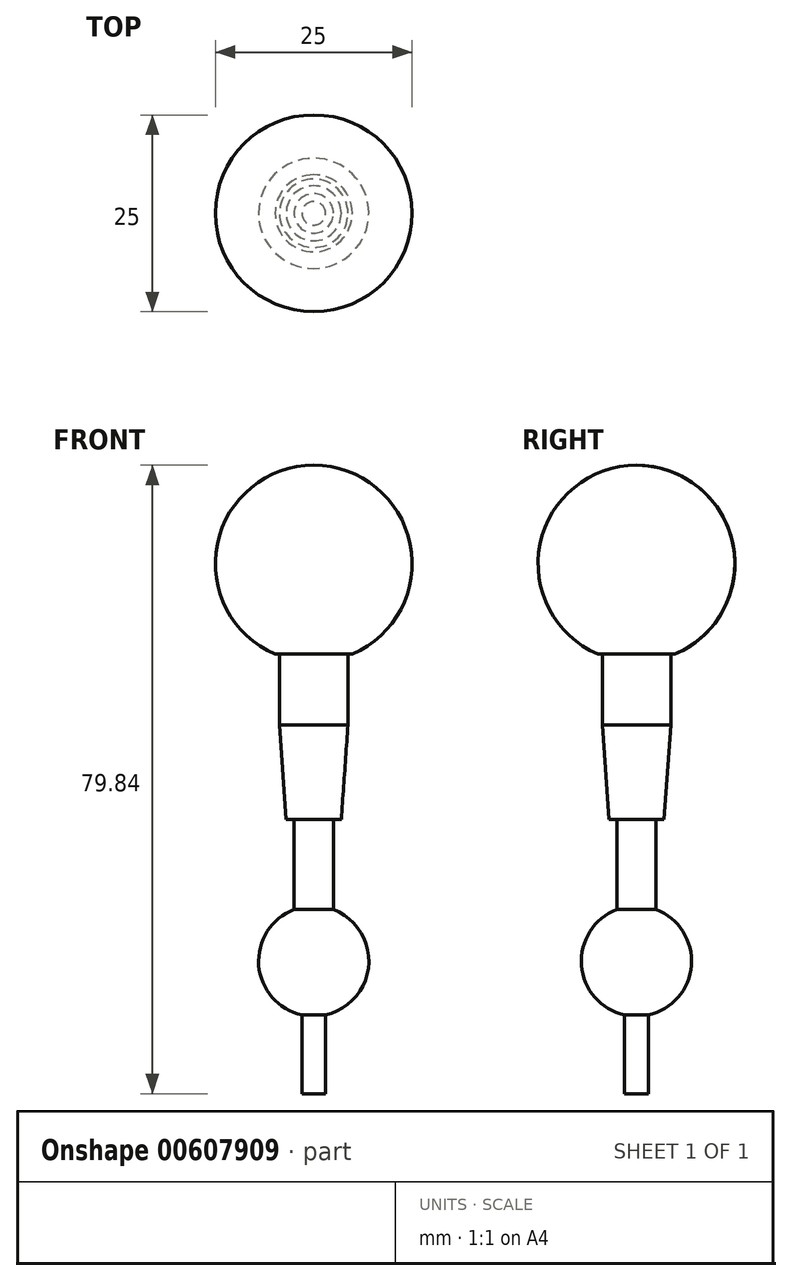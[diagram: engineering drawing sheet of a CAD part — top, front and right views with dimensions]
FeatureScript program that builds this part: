
annotation { "Feature Type Name" : "Feature", "Feature Type Description" : "" }
export const myFeature = defineFeature(function(context is Context, id is Id, definition is map)
    precondition{}
    {
        {
            var Q0;
            Q0=qCreatedBy(makeId("Right.planeOp"),FACE);
            var sketch = newSketch(context, id + "F0", { "sketchPlane" : qUnion([Q0])});
            skLineSegment(sketch, "E0", {"start": v(0, 70) * mm, "end": v(0, 0) * mm});
            skArc(sketch, "E1", {"start": v(0, 70) * mm, "mid": v(12.5, 57.5) * mm, "end": v(0, 45) * mm});
            skLineSegment(sketch, "E2", {"start": v(0, 46) * mm, "end": v(4.9, 46) * mm});
            skLineSegment(sketch, "E3", {"start": v(4.35, 46) * mm, "end": v(4.35, 37) * mm});
            skLineSegment(sketch, "E4", {"start": v(4.35, 37) * mm, "end": v(3.5, 25) * mm});
            skLineSegment(sketch, "E5", {"start": v(3.5, 25) * mm, "end": v(0, 25) * mm});
            skLineSegment(sketch, "E6", {"start": v(2.5, 25) * mm, "end": v(2.5, 13.54) * mm});
            skLineSegment(sketch, "E7", {"start": v(2.5, 13.54) * mm, "end": v(0, 13.54) * mm});
            skArc(sketch, "E8", {"start": v(0, 0) * mm, "mid": v(7, 7) * mm, "end": v(0, 14) * mm});
            skLineSegment(sketch, "E9.bottom", {"start": v(0, 0.16) * mm, "end": v(1.5, 0.16) * mm});
            skLineSegment(sketch, "E9.top", {"start": v(0, -9.84) * mm, "end": v(1.5, -9.84) * mm});
            skLineSegment(sketch, "E9.left", {"start": v(0, 0.16) * mm, "end": v(0, -9.84) * mm});
            skLineSegment(sketch, "E9.right", {"start": v(1.5, 0.16) * mm, "end": v(1.5, -9.84) * mm});
            skSolve(sketch);
        }
        {
            var Q0;
            {var subQ0=sQuery(id+"F0.wireOp",EDGE,"E1");var subQ1=sQuery(id+"F0.wireOp",EDGE,"E0");var subQ2=makeQuery(id+"F0.imprint","INTERSECT",VERTEX,{"disambiguationData":[OD(0.0)],"derivedFrom":[subQ1,subQ0]});Q0=makeQuery(id+"F0.imprint","IMPRINT",FACE,{"disambiguationData":[TD([[makeQuery(id+"F0.imprint","IMPRINT",EDGE,{"disambiguationData":[TD([[subQ2,-1.0]])],"derivedFrom":subQ1}),1.0]])]});}
            var Q1;
            {var subQ0=sQuery(id+"F0.wireOp",EDGE,"E4");Q1=makeQuery(id+"F0.imprint","IMPRINT",FACE,{"disambiguationData":[TD([[makeQuery(id+"F0.imprint","IMPRINT",EDGE,{"derivedFrom":subQ0}),-1.0]])]});}
            var Q2;
            {var subQ5=sQuery(id+"F0.wireOp",EDGE,"E6");Q2=makeQuery(id+"F0.imprint","IMPRINT",FACE,{"disambiguationData":[TD([[makeQuery(id+"F0.imprint","IMPRINT",EDGE,{"derivedFrom":subQ5}),-1.0]])]});}
            var Q3;
            {var subQ2=sQuery(id+"F0.wireOp",EDGE,"E7");Q3=makeQuery(id+"F0.imprint","IMPRINT",FACE,{"disambiguationData":[TD([[makeQuery(id+"F0.imprint","IMPRINT",EDGE,{"derivedFrom":subQ2}),1.0]])]});}
            var Q4;
            {var subQ0=sQuery(id+"F0.wireOp",EDGE,"E7");Q4=makeQuery(id+"F0.imprint","IMPRINT",FACE,{"disambiguationData":[TD([[makeQuery(id+"F0.imprint","IMPRINT",EDGE,{"derivedFrom":subQ0}),-1.0]])]});}
            var Q5;
            {var subQ0=sQuery(id+"F0.wireOp",EDGE,"E1");var subQ1=sQuery(id+"F0.wireOp",EDGE,"E0");var subQ2=makeQuery(id+"F0.imprint","INTERSECT",VERTEX,{"disambiguationData":[OD(1.0)],"derivedFrom":[subQ1,subQ0]});Q5=makeQuery(id+"F0.imprint","IMPRINT",FACE,{"disambiguationData":[TD([[makeQuery(id+"F0.imprint","IMPRINT",EDGE,{"disambiguationData":[TD([[subQ2,1.0]])],"derivedFrom":subQ1}),1.0]])]});}
            var Q6;
            {var subQ4=sQuery(id+"F0.wireOp",EDGE,"E9.top");Q6=makeQuery(id+"F0.imprint","IMPRINT",FACE,{"disambiguationData":[TD([[makeQuery(id+"F0.imprint","IMPRINT",EDGE,{"derivedFrom":subQ4}),1.0]])]});}
            var Q7;
            {var subQ3=sQuery(id+"F0.wireOp",EDGE,"E9.bottom");Q7=makeQuery(id+"F0.imprint","IMPRINT",FACE,{"disambiguationData":[TD([[makeQuery(id+"F0.imprint","IMPRINT",EDGE,{"derivedFrom":subQ3}),-1.0]])]});}
            var Q8;
            Q8=sQuery(id+"F0.wireOp",EDGE,"E0");
            revolve(context, id + "F1", {"entities" : qUnion([Q0, Q1, Q2, Q3, Q4, Q5, Q6, Q7]), "axis" : qUnion([Q8]), "revolveType" : RevolveType.FULL});
        }
    });
